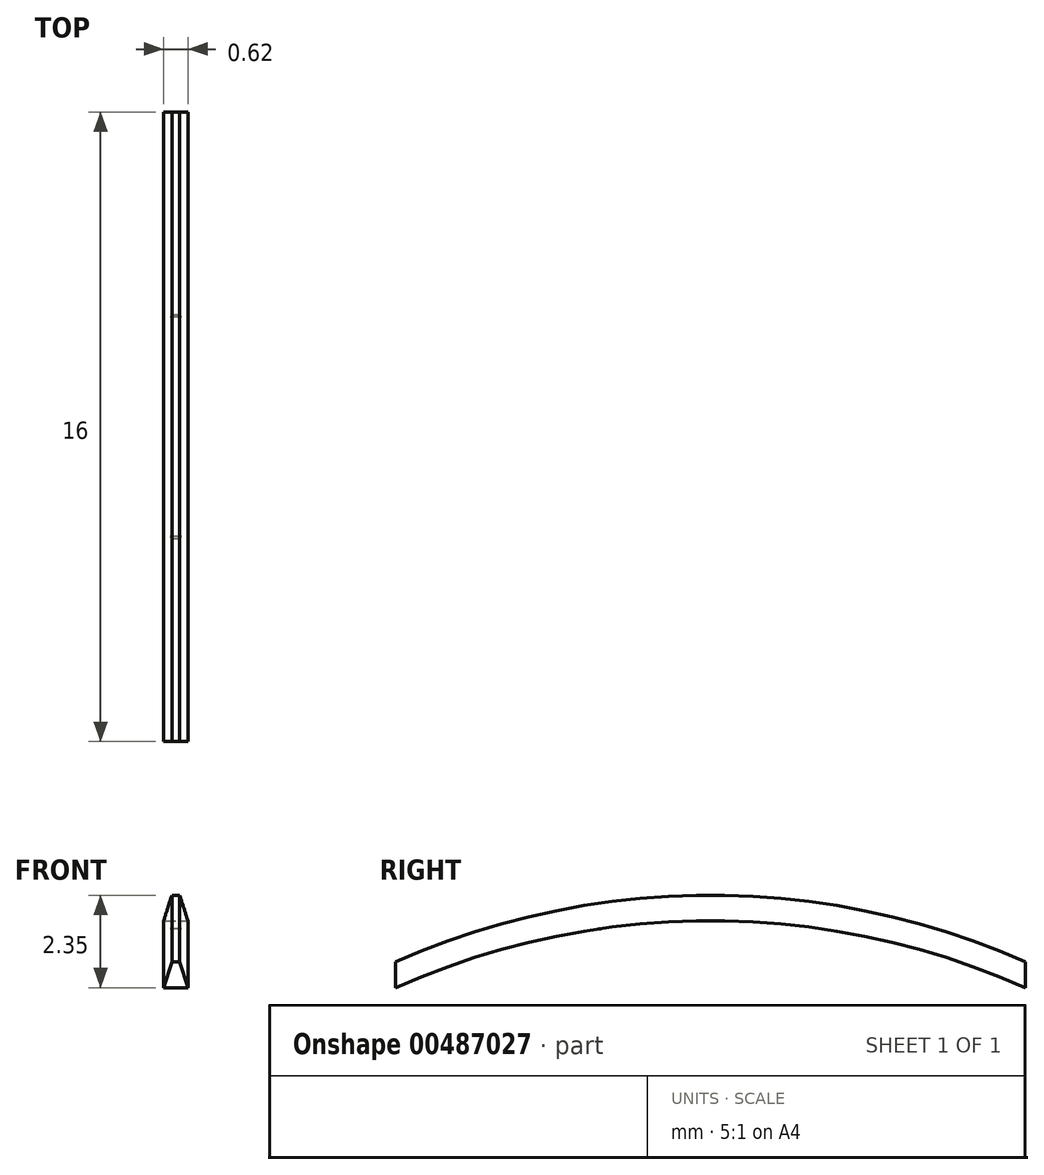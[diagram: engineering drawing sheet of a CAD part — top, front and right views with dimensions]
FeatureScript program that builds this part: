
annotation { "Feature Type Name" : "Feature", "Feature Type Description" : "" }
export const myFeature = defineFeature(function(context is Context, id is Id, definition is map)
    precondition{}
    {
        {
            var Q0;
            Q0=qCreatedBy(makeId("Right.planeOp"),FACE);
            var sketch = newSketch(context, id + "F0", { "sketchPlane" : qUnion([Q0])});
            skLineSegment(sketch, "E0", {"start": v(0, 0) * mm, "end": v(16, 0) * mm, "construction": true});
            skLineSegment(sketch, "E1", {"start": v(8, 1.7) * mm, "end": v(8, 0) * mm, "construction": true});
            skArc(sketch, "E2", {"start": v(16, 0) * mm, "mid": v(8, 1.7) * mm, "end": v(0, 0) * mm});
            skSolve(sketch);
        }
        {
            var Q0;
            Q0=qCreatedBy(makeId("Front.planeOp"),FACE);
            var sketch = newSketch(context, id + "F1", { "sketchPlane" : qUnion([Q0])});
            skLineSegment(sketch, "E3", {"start": v(-0.1, 0.65) * mm, "end": v(0.1, 0.65) * mm});
            skLineSegment(sketch, "E4", {"start": v(-0.3, 0) * mm, "end": v(0.3, 0) * mm});
            skLineSegment(sketch, "E5", {"start": v(-0.1, 0.65) * mm, "end": v(-0.3, 0) * mm});
            skLineSegment(sketch, "E6", {"start": v(0.1, 0.65) * mm, "end": v(0.3, 0) * mm});
            skSolve(sketch);
        }
        {
            var Q0;
            Q0=makeQuery(id+"F1.imprint","IMPRINT",FACE,{"disambiguationData":[TD([[makeQuery(id+"F1.imprint","IMPRINT",EDGE,{"derivedFrom":sQuery(id+"F1.wireOp",EDGE,"E3")}),-1.0]])]});
            var Q1;
            Q1=sQuery(id+"F1.wireOp",EDGE,"E6");
            var Q2;
            Q2=sQuery(id+"F0.wireOp",EDGE,"E2");
            sweep(context, id + "F2", {"profiles" : qUnion([Q0]), "surfaceProfiles" : qUnion([Q1]), "path" : qUnion([Q2]), "keepProfileOrientation" : true});
        }
        {
            var Q0;
            Q0=qCreatedBy(makeId("Top.planeOp"),FACE);
            var sketch = newSketch(context, id + "F3", { "sketchPlane" : qUnion([Q0])});
            skCircle(sketch, "E7", {"center": v(0, 5.36) * mm, "radius": 0.2 * mm});
            skPoint(sketch, "E8", {"position": v(0, 4.8) * mm});
            skCircle(sketch, "E9", {"center": v(0, 10.64) * mm, "radius": 0.2 * mm});
            skPoint(sketch, "E10", {"position": v(0, 8) * mm});
            skSolve(sketch);
        }
        {
            var Q0;
            Q0 = qSketchRegion(id + "F3", true);
            var Q1;
            Q1=makeQuery(id+"F2.opSweep","SWEPT_FACE",FACE,{"disambiguationData":[OSD([sQuery(id+"F0.wireOp",EDGE,"E2"),sQuery(id+"F1.wireOp",EDGE,"E4")])]});
            extrude(context, id + "F4", {"entities" : qUnion([Q0]), "operationType" : NewBodyOperationType.REMOVE, "depth" : 1.5 * mm, "endBoundEntityFace" : qUnion([Q1]), "offsetDistance" : 25.4 * mm});
        }
    });
